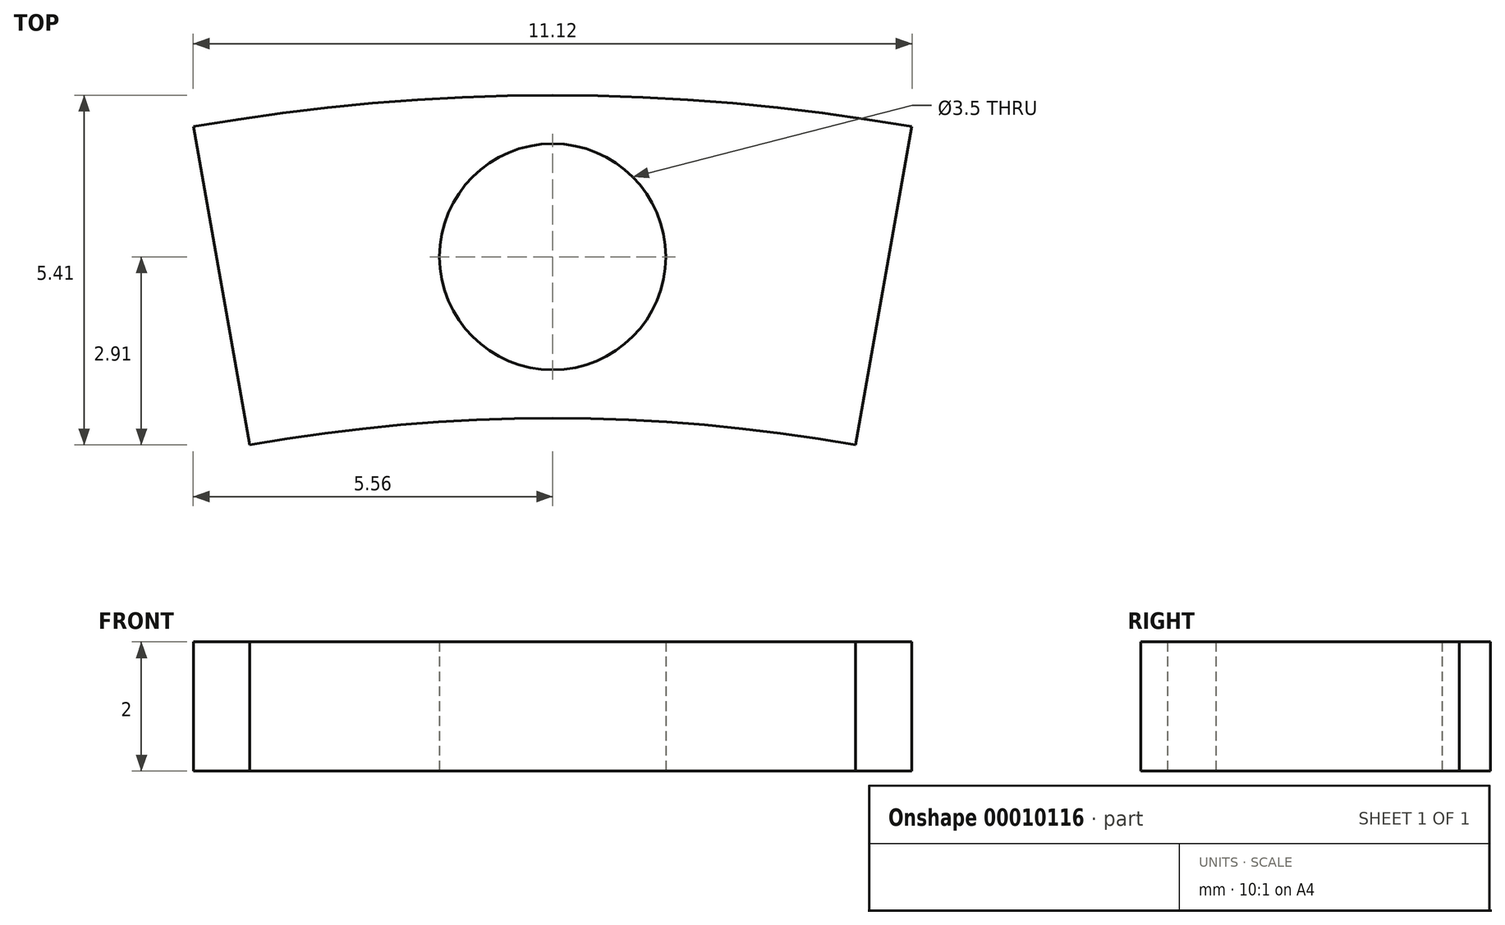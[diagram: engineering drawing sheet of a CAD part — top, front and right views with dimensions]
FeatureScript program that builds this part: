
annotation { "Feature Type Name" : "Feature", "Feature Type Description" : "" }
export const myFeature = defineFeature(function(context is Context, id is Id, definition is map)
    precondition{}
    {
        {
            var Q0;
            Q0=qCreatedBy(makeId("Top.planeOp"),FACE);
            var sketch = newSketch(context, id + "F0", { "sketchPlane" : qUnion([Q0])});
            skArc(sketch, "E0", {"start": v(5.56, 31.51) * mm, "mid": v(0, 32) * mm, "end": v(-5.56, 31.51) * mm});
            skArc(sketch, "E1", {"start": v(4.69, 26.59) * mm, "mid": v(0, 27) * mm, "end": v(-4.69, 26.59) * mm});
            skLineSegment(sketch, "E2", {"start": v(0, 0) * mm, "end": v(-4.69, 26.59) * mm, "construction": true});
            skLineSegment(sketch, "E3", {"start": v(-4.69, 26.59) * mm, "end": v(-5.56, 31.51) * mm});
            skLineSegment(sketch, "E4", {"start": v(0, 0) * mm, "end": v(4.69, 26.59) * mm, "construction": true});
            skLineSegment(sketch, "E5", {"start": v(4.69, 26.59) * mm, "end": v(5.56, 31.51) * mm});
            skLineSegment(sketch, "E6", {"start": v(0, 0) * mm, "end": v(0, 27) * mm, "construction": true});
            skLineSegment(sketch, "E7", {"start": v(-4.69, 26.59) * mm, "end": v(0, 27) * mm, "construction": true});
            skLineSegment(sketch, "E8", {"start": v(0, 27) * mm, "end": v(4.69, 26.59) * mm, "construction": true});
            skLineSegment(sketch, "E9", {"start": v(0, 27) * mm, "end": v(0, 29.5) * mm, "construction": true});
            skLineSegment(sketch, "E10", {"start": v(0, 29.5) * mm, "end": v(0, 32) * mm, "construction": true});
            skCircle(sketch, "E11", {"center": v(0, 29.5) * mm, "radius": 1.75 * mm});
            skSolve(sketch);
        }
        {
            var Q0;
            Q0=makeQuery(id+"F0.imprint","IMPRINT",FACE,{"disambiguationData":[TD([[makeQuery(id+"F0.imprint","IMPRINT",EDGE,{"derivedFrom":sQuery(id+"F0.wireOp",EDGE,"E0")}),1.0]])]});
            extrude(context, id + "F1", {"entities" : qUnion([Q0]), "depth" : 2 * mm});
        }
    });
